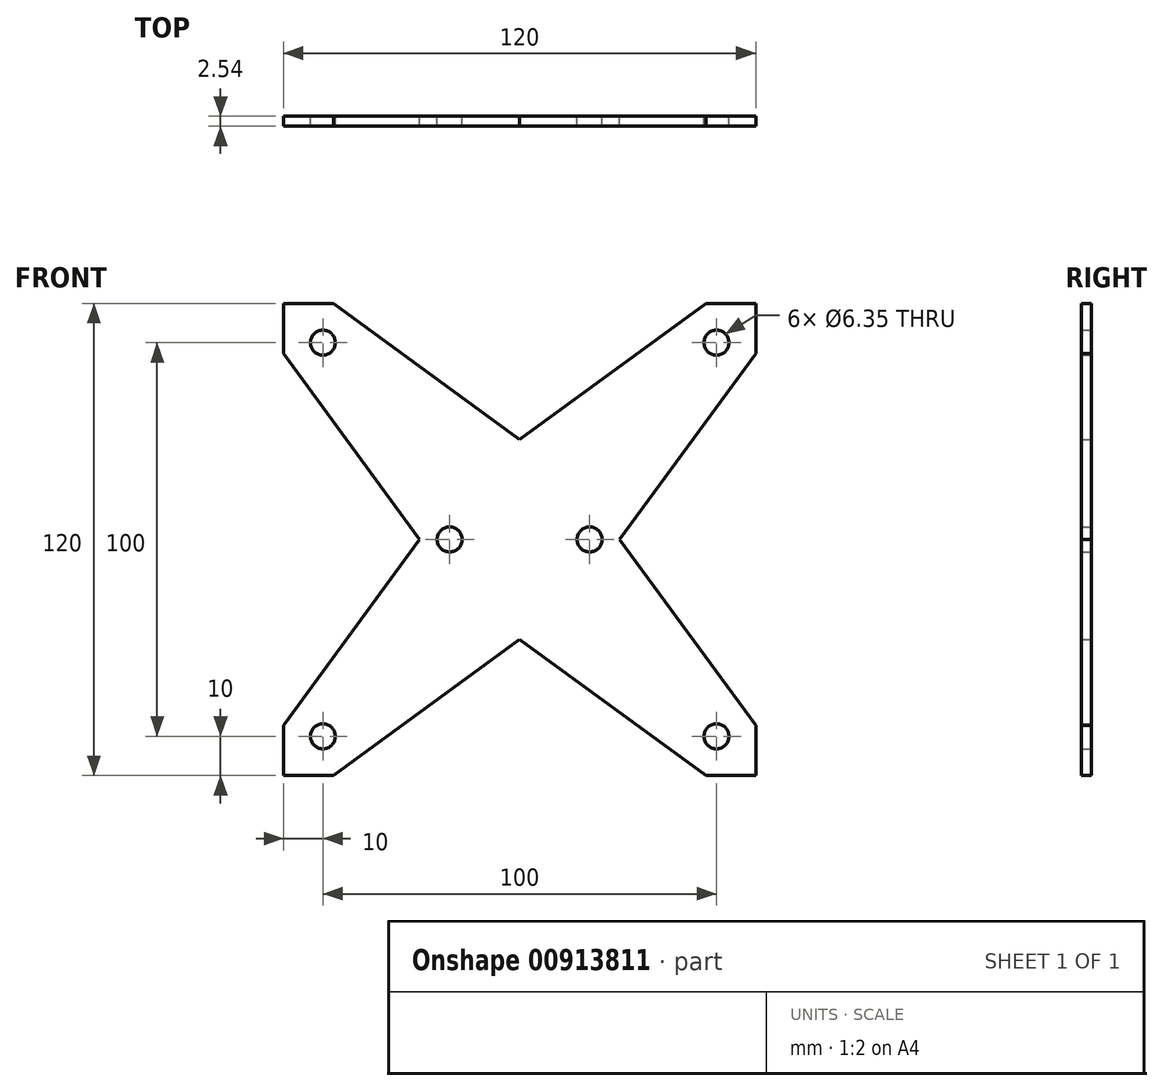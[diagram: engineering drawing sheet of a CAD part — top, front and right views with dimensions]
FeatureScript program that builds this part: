
annotation { "Feature Type Name" : "Feature", "Feature Type Description" : "" }
export const myFeature = defineFeature(function(context is Context, id is Id, definition is map)
    precondition{}
    {
        {
            var Q0;
            Q0=qCreatedBy(makeId("Front.planeOp"),FACE);
            var sketch = newSketch(context, id + "F0", { "sketchPlane" : qUnion([Q0])});
            skLineSegment(sketch, "E0.bottom", {"start": v(60, 60) * mm, "end": v(47.3, 60) * mm});
            skLineSegment(sketch, "E0.top", {"start": v(60, -60) * mm, "end": v(47.3, -60) * mm});
            skLineSegment(sketch, "E0.left", {"start": v(60, 60) * mm, "end": v(60, 47.3) * mm});
            skLineSegment(sketch, "E0.right", {"start": v(-60, 60) * mm, "end": v(-60, 47.3) * mm});
            skPoint(sketch, "E0.middle", {"position": v(0, 0) * mm});
            skCircle(sketch, "E1", {"center": v(-50, 50) * mm, "radius": 3.18 * mm});
            skCircle(sketch, "E2", {"center": v(50, 50) * mm, "radius": 3.18 * mm});
            skCircle(sketch, "E3", {"center": v(50, -50) * mm, "radius": 3.18 * mm});
            skCircle(sketch, "E4", {"center": v(-50, -50) * mm, "radius": 3.18 * mm});
            skLineSegment(sketch, "E5", {"start": v(-60, 47.3) * mm, "end": v(-25.4, 0) * mm});
            skLineSegment(sketch, "E6", {"start": v(-25.4, 0) * mm, "end": v(-60, -47.3) * mm});
            skLineSegment(sketch, "E7.trimOffspring", {"start": v(-60, -47.3) * mm, "end": v(-60, -60) * mm});
            skLineSegment(sketch, "E8", {"start": v(0, 0) * mm, "end": v(0, 91.14) * mm, "construction": true});
            skPoint(sketch, "E8.endSnap0", {"position": v(0, 60) * mm});
            skLineSegment(sketch, "E9.MirrorCS", {"start": v(60, 47.3) * mm, "end": v(25.4, 0) * mm});
            skLineSegment(sketch, "E10.MirrorCS", {"start": v(25.4, 0) * mm, "end": v(60, -47.3) * mm});
            skLineSegment(sketch, "E11", {"start": v(0, 0) * mm, "end": v(162.36, 0) * mm, "construction": true});
            skLineSegment(sketch, "E12.trimOffspring", {"start": v(60, -47.3) * mm, "end": v(60, -60) * mm});
            skLineSegment(sketch, "E13", {"start": v(-47.3, 60) * mm, "end": v(0, 25.4) * mm});
            skLineSegment(sketch, "E14", {"start": v(0, 25.4) * mm, "end": v(47.3, 60) * mm});
            skLineSegment(sketch, "E15.MirrorCS", {"start": v(0, -25.4) * mm, "end": v(47.3, -60) * mm});
            skLineSegment(sketch, "E16.MirrorCS", {"start": v(-47.3, -60) * mm, "end": v(0, -25.4) * mm});
            skLineSegment(sketch, "E17.trimOffspring", {"start": v(-47.3, 60) * mm, "end": v(-60, 60) * mm});
            skLineSegment(sketch, "E18.trimOffspring", {"start": v(-47.3, -60) * mm, "end": v(-60, -60) * mm});
            skCircle(sketch, "E19", {"center": v(-17.78, 0) * mm, "radius": 3.18 * mm});
            skCircle(sketch, "E20.MirrorC", {"center": v(17.78, 0) * mm, "radius": 3.18 * mm});
            skLineSegment(sketch, "E21", {"start": v(-12.7, 12.15) * mm, "end": v(-12.7, 0) * mm});
            skLineSegment(sketch, "E22.MirrorCS", {"start": v(12.7, 12.15) * mm, "end": v(12.7, 0) * mm});
            skSolve(sketch);
        }
        {
            var Q0;
            Q0 = qSketchRegion(id + "F0", true);
            extrude(context, id + "F1", {"entities" : qUnion([Q0]), "depth" : 2.54 * mm, "offsetDistance" : 25.4 * mm});
        }
    });
